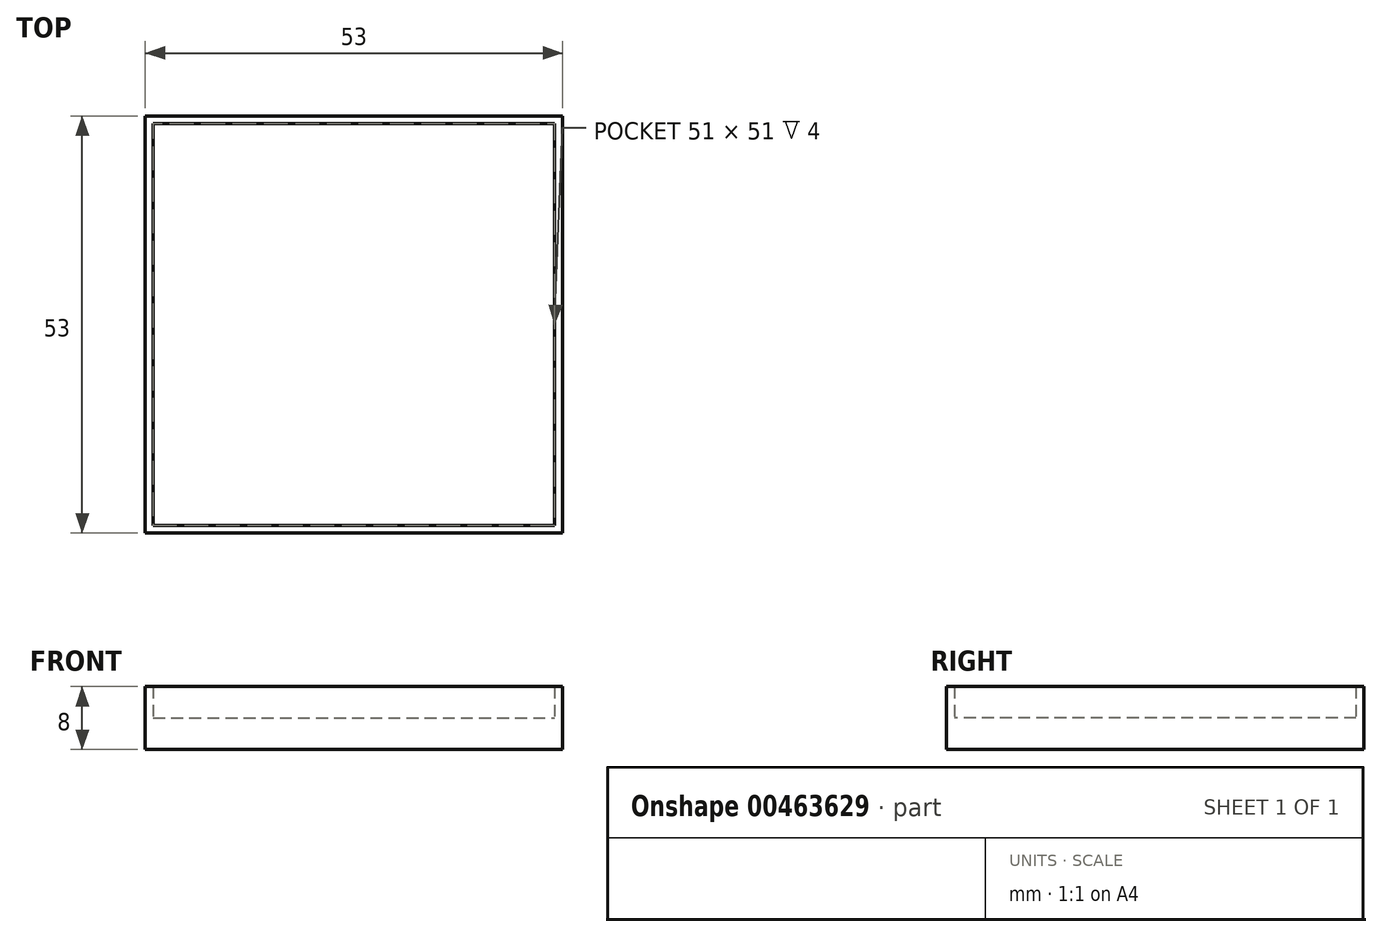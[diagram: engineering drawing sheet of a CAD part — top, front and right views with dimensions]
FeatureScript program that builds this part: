
annotation { "Feature Type Name" : "Feature", "Feature Type Description" : "" }
export const myFeature = defineFeature(function(context is Context, id is Id, definition is map)
    precondition{}
    {
        {
            var Q0;
            Q0=qCreatedBy(makeId("Top.planeOp"),FACE);
            var sketch = newSketch(context, id + "F0", { "sketchPlane" : qUnion([Q0])});
            skLineSegment(sketch, "E0.bottom", {"start": v(0, 0) * mm, "end": v(53, 0) * mm});
            skLineSegment(sketch, "E0.top", {"start": v(0, 53) * mm, "end": v(53, 53) * mm});
            skLineSegment(sketch, "E0.left", {"start": v(0, 0) * mm, "end": v(0, 53) * mm});
            skLineSegment(sketch, "E0.right", {"start": v(53, 0) * mm, "end": v(53, 53) * mm});
            skLineSegment(sketch, "E1", {"start": v(1, 53) * mm, "end": v(1, 0) * mm});
            skLineSegment(sketch, "E2", {"start": v(0, 1) * mm, "end": v(53, 1) * mm});
            skLineSegment(sketch, "E3", {"start": v(52, 0) * mm, "end": v(52, 53) * mm});
            skLineSegment(sketch, "E4", {"start": v(0, 52) * mm, "end": v(53, 52) * mm});
            skSolve(sketch);
        }
        {
            var Q0;
            {var subQ0=sQuery(id+"F0.wireOp",EDGE,"E4");var subQ1=sQuery(id+"F0.wireOp",EDGE,"E1");var subQ2=makeQuery(id+"F0.imprint","INTERSECT",VERTEX,{"derivedFrom":[subQ1,subQ0]});Q0=makeQuery(id+"F0.imprint","IMPRINT",FACE,{"disambiguationData":[TD([[makeQuery(id+"F0.imprint","IMPRINT",EDGE,{"disambiguationData":[TD([[subQ2,-1.0]])],"derivedFrom":subQ1}),1.0]])]});}
            extrude(context, id + "F1", {"entities" : qUnion([Q0]), "depth" : 4 * mm});
        }
        {
            var Q0;
            {var subQ0=sQuery(id+"F0.wireOp",EDGE,"E2");var subQ1=sQuery(id+"F0.wireOp",EDGE,"E0.left");var subQ2=makeQuery(id+"F0.imprint","INTERSECT",VERTEX,{"derivedFrom":[subQ1,subQ0]});Q0=makeQuery(id+"F0.imprint","IMPRINT",FACE,{"disambiguationData":[TD([[makeQuery(id+"F0.imprint","IMPRINT",EDGE,{"disambiguationData":[TD([[subQ2,-1.0]])],"derivedFrom":subQ1}),-1.0]])]});}
            var Q1;
            {var subQ0=sQuery(id+"F0.wireOp",EDGE,"E0.left");var subQ1=sQuery(id+"F0.wireOp",EDGE,"E0.top");var subQ2=makeQuery(id+"F0.imprint","INTERSECT",VERTEX,{"derivedFrom":[subQ1,subQ0]});Q1=makeQuery(id+"F0.imprint","IMPRINT",FACE,{"disambiguationData":[TD([[makeQuery(id+"F0.imprint","IMPRINT",EDGE,{"disambiguationData":[TD([[subQ2,-1.0]])],"derivedFrom":subQ1}),-1.0]])]});}
            var Q2;
            {var subQ0=sQuery(id+"F0.wireOp",EDGE,"E1");var subQ1=sQuery(id+"F0.wireOp",EDGE,"E0.top");var subQ2=makeQuery(id+"F0.imprint","INTERSECT",VERTEX,{"derivedFrom":[subQ1,subQ0]});Q2=makeQuery(id+"F0.imprint","IMPRINT",FACE,{"disambiguationData":[TD([[makeQuery(id+"F0.imprint","IMPRINT",EDGE,{"disambiguationData":[TD([[subQ2,-1.0]])],"derivedFrom":subQ1}),-1.0]])]});}
            var Q3;
            {var subQ0=sQuery(id+"F0.wireOp",EDGE,"E0.right");var subQ1=sQuery(id+"F0.wireOp",EDGE,"E0.top");var subQ2=makeQuery(id+"F0.imprint","INTERSECT",VERTEX,{"derivedFrom":[subQ1,subQ0]});Q3=makeQuery(id+"F0.imprint","IMPRINT",FACE,{"disambiguationData":[TD([[makeQuery(id+"F0.imprint","IMPRINT",EDGE,{"disambiguationData":[TD([[subQ2,1.0]])],"derivedFrom":subQ1}),-1.0]])]});}
            var Q4;
            {var subQ0=sQuery(id+"F0.wireOp",EDGE,"E2");var subQ1=sQuery(id+"F0.wireOp",EDGE,"E0.right");var subQ2=makeQuery(id+"F0.imprint","INTERSECT",VERTEX,{"derivedFrom":[subQ1,subQ0]});Q4=makeQuery(id+"F0.imprint","IMPRINT",FACE,{"disambiguationData":[TD([[makeQuery(id+"F0.imprint","IMPRINT",EDGE,{"disambiguationData":[TD([[subQ2,-1.0]])],"derivedFrom":subQ1}),1.0]])]});}
            var Q5;
            {var subQ0=sQuery(id+"F0.wireOp",EDGE,"E0.right");var subQ1=sQuery(id+"F0.wireOp",EDGE,"E0.bottom");var subQ2=makeQuery(id+"F0.imprint","INTERSECT",VERTEX,{"derivedFrom":[subQ1,subQ0]});Q5=makeQuery(id+"F0.imprint","IMPRINT",FACE,{"disambiguationData":[TD([[makeQuery(id+"F0.imprint","IMPRINT",EDGE,{"disambiguationData":[TD([[subQ2,1.0]])],"derivedFrom":subQ1}),1.0]])]});}
            var Q6;
            {var subQ0=sQuery(id+"F0.wireOp",EDGE,"E1");var subQ1=sQuery(id+"F0.wireOp",EDGE,"E0.bottom");var subQ2=makeQuery(id+"F0.imprint","INTERSECT",VERTEX,{"derivedFrom":[subQ1,subQ0]});Q6=makeQuery(id+"F0.imprint","IMPRINT",FACE,{"disambiguationData":[TD([[makeQuery(id+"F0.imprint","IMPRINT",EDGE,{"disambiguationData":[TD([[subQ2,-1.0]])],"derivedFrom":subQ1}),1.0]])]});}
            var Q7;
            {var subQ0=sQuery(id+"F0.wireOp",EDGE,"E0.left");var subQ1=sQuery(id+"F0.wireOp",EDGE,"E0.bottom");var subQ2=makeQuery(id+"F0.imprint","INTERSECT",VERTEX,{"derivedFrom":[subQ1,subQ0]});Q7=makeQuery(id+"F0.imprint","IMPRINT",FACE,{"disambiguationData":[TD([[makeQuery(id+"F0.imprint","IMPRINT",EDGE,{"disambiguationData":[TD([[subQ2,-1.0]])],"derivedFrom":subQ1}),1.0]])]});}
            extrude(context, id + "F2", {"entities" : qUnion([Q0, Q1, Q2, Q3, Q4, Q5, Q6, Q7]), "operationType" : NewBodyOperationType.ADD, "depth" : 8 * mm});
        }
    });
